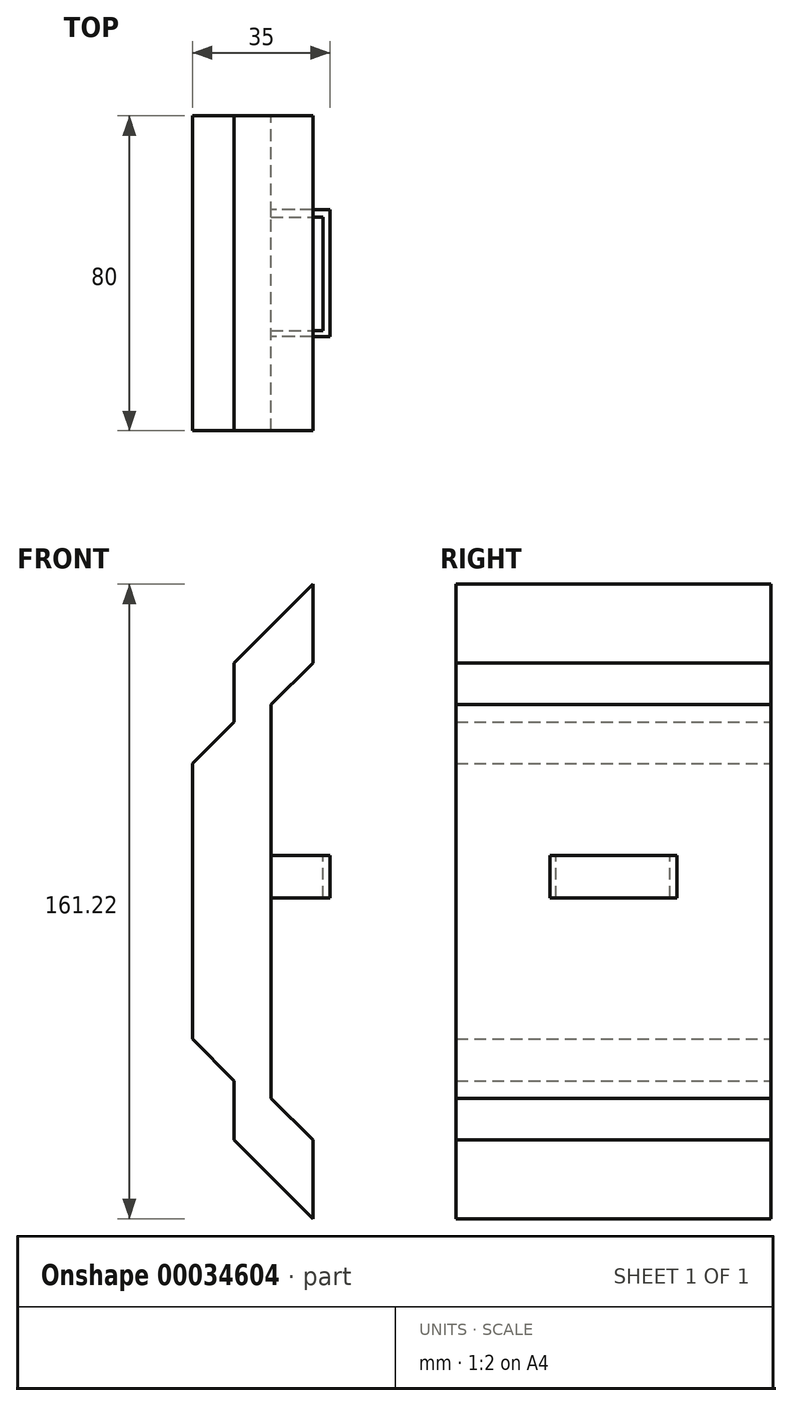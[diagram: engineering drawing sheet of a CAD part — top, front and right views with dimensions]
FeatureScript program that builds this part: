
annotation { "Feature Type Name" : "Feature", "Feature Type Description" : "" }
export const myFeature = defineFeature(function(context is Context, id is Id, definition is map)
    precondition{}
    {
        {
            var Q0;
            Q0=qCreatedBy(makeId("Front.planeOp"),FACE);
            var sketch = newSketch(context, id + "F0", { "sketchPlane" : qUnion([Q0])});
            skLineSegment(sketch, "E0", {"start": v(-33.15, 28.72) * mm, "end": v(-33.15, -41.28) * mm});
            skLineSegment(sketch, "E1", {"start": v(-33.15, -41.28) * mm, "end": v(-22.54, -51.89) * mm});
            skLineSegment(sketch, "E2", {"start": v(-22.54, -51.89) * mm, "end": v(-22.54, -66.89) * mm});
            skLineSegment(sketch, "E3", {"start": v(-22.54, -66.89) * mm, "end": v(-2.54, -86.89) * mm});
            skLineSegment(sketch, "E4", {"start": v(-2.54, -86.89) * mm, "end": v(-2.54, -66.89) * mm});
            skLineSegment(sketch, "E5", {"start": v(-2.54, -66.89) * mm, "end": v(-13.15, -56.28) * mm});
            skLineSegment(sketch, "E6", {"start": v(-13.15, -56.28) * mm, "end": v(-13.15, 43.72) * mm});
            skLineSegment(sketch, "E7", {"start": v(-13.15, 43.72) * mm, "end": v(-2.54, 54.33) * mm});
            skLineSegment(sketch, "E8", {"start": v(-2.54, 54.33) * mm, "end": v(-2.54, 74.33) * mm});
            skLineSegment(sketch, "E9", {"start": v(-2.54, 74.33) * mm, "end": v(-22.54, 54.33) * mm});
            skLineSegment(sketch, "E10", {"start": v(-22.54, 54.33) * mm, "end": v(-22.54, 39.33) * mm});
            skLineSegment(sketch, "E11", {"start": v(-22.54, 39.33) * mm, "end": v(-33.15, 28.72) * mm});
            skSolve(sketch);
        }
        {
            var Q0;
            Q0=makeQuery(id+"F0.imprint","IMPRINT",FACE,{"disambiguationData":[TD([[makeQuery(id+"F0.imprint","IMPRINT",EDGE,{"derivedFrom":sQuery(id+"F0.wireOp",EDGE,"E0")}),1.0]])]});
            extrude(context, id + "F1", {"entities" : qUnion([Q0]), "depth" : 80 * mm});
        }
        {
            var Q0;
            Q0=makeQuery(id+"F1.opExtrude","SWEPT_FACE",FACE,{"disambiguationData":[OSD([sQuery(id+"F0.wireOp",EDGE,"E6")])]});
            var sketch = newSketch(context, id + "F2", { "sketchPlane" : qUnion([Q0])});
            skLineSegment(sketch, "E12.rect.bottom", {"start": v(-56.15, 5.36) * mm, "end": v(-23.85, 5.36) * mm});
            skLineSegment(sketch, "E12.rect.top", {"start": v(-56.15, -5.36) * mm, "end": v(-23.85, -5.36) * mm});
            skLineSegment(sketch, "E12.rect.left", {"start": v(-56.15, 5.36) * mm, "end": v(-56.15, -5.36) * mm});
            skLineSegment(sketch, "E12.rect.right", {"start": v(-23.85, 5.36) * mm, "end": v(-23.85, -5.36) * mm});
            skPoint(sketch, "E12.rect.middle", {"position": v(-40, 0) * mm});
            skPoint(sketch, "E12.rect.middle.positionSnap0", {"position": v(-40, 43.72) * mm});
            skPoint(sketch, "E12.rect.centerSnap0", {"position": v(-40, 43.72) * mm});
            skSolve(sketch);
        }
        {
            var Q0;
            Q0 = qSketchRegion(id + "F2", true);
            extrude(context, id + "F3", {"entities" : qUnion([Q0]), "operationType" : NewBodyOperationType.ADD, "depth" : 15 * mm});
        }
        {
            var Q0;
            Q0=makeQuery(id+"F3.opExtrude","SWEPT_FACE",FACE,{"disambiguationData":[OSD([sQuery(id+"F2.wireOp",EDGE,"E12.rect.bottom")])]});
            var sketch = newSketch(context, id + "F4", { "sketchPlane" : qUnion([Q0])});
            skLineSegment(sketch, "E13.bottom", {"start": v(-13.15, -25.72) * mm, "end": v(0, -25.72) * mm});
            skLineSegment(sketch, "E13.top", {"start": v(-13.15, -54.63) * mm, "end": v(0, -54.63) * mm});
            skLineSegment(sketch, "E13.left", {"start": v(-13.15, -25.72) * mm, "end": v(-13.15, -54.63) * mm});
            skLineSegment(sketch, "E13.right", {"start": v(0, -25.72) * mm, "end": v(0, -54.63) * mm});
            skSolve(sketch);
        }
        {
            var Q0;
            Q0 = qSketchRegion(id + "F4", true);
            extrude(context, id + "F5", {"entities" : qUnion([Q0]), "operationType" : NewBodyOperationType.REMOVE, "oppositeDirection" : true, "depth" : 25 * mm});
        }
    });
